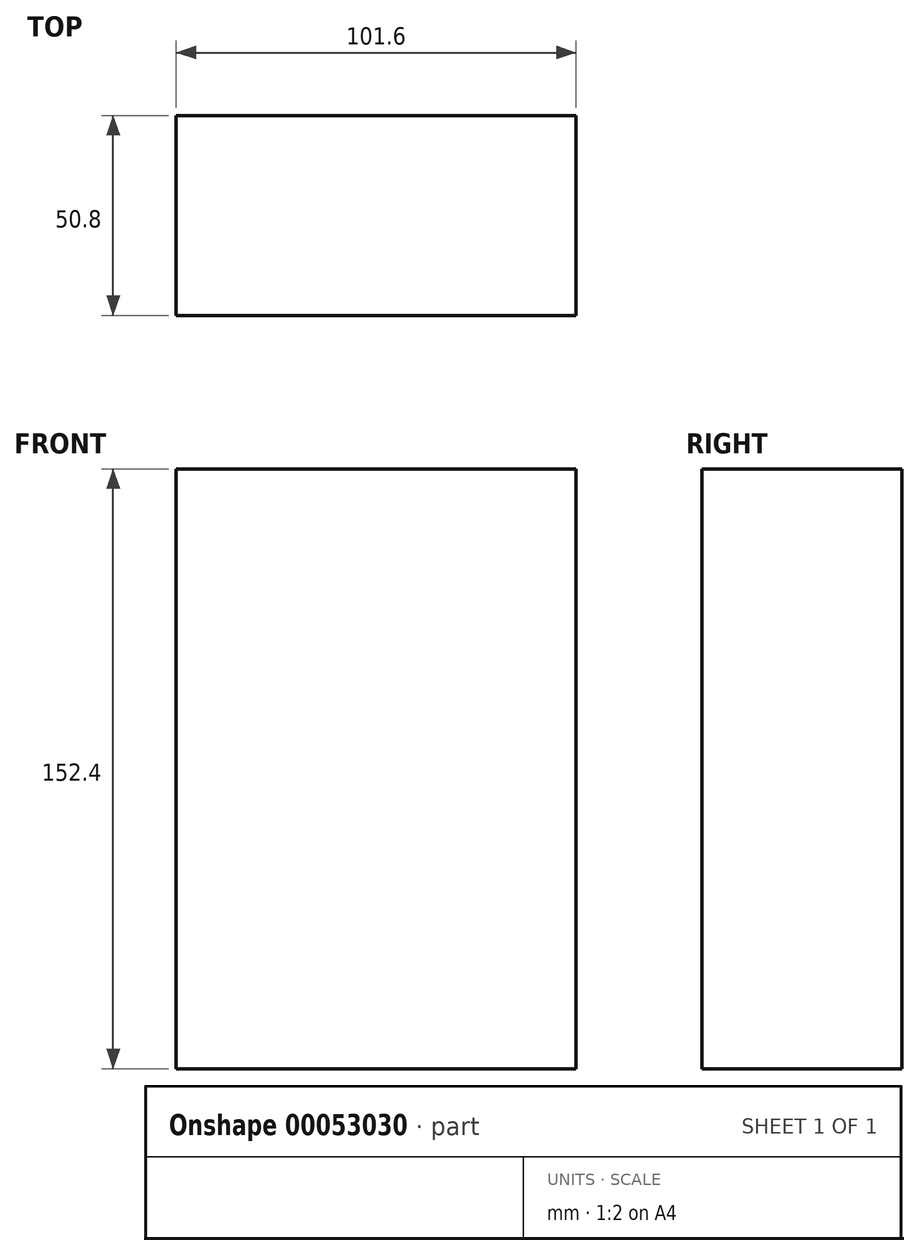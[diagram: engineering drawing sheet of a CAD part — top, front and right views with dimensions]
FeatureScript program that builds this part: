
annotation { "Feature Type Name" : "Feature", "Feature Type Description" : "" }
export const myFeature = defineFeature(function(context is Context, id is Id, definition is map)
    precondition{}
    {
        {
            var Q0;
            Q0=qCreatedBy(makeId("Top.planeOp"),FACE);
            var sketch = newSketch(context, id + "F0", { "sketchPlane" : qUnion([Q0])});
            skLineSegment(sketch, "E0.bottom", {"start": v(0, 0) * mm, "end": v(-101.6, 0) * mm});
            skLineSegment(sketch, "E0.top", {"start": v(0, 50.8) * mm, "end": v(-101.6, 50.8) * mm});
            skLineSegment(sketch, "E0.left", {"start": v(0, 0) * mm, "end": v(0, 50.8) * mm});
            skLineSegment(sketch, "E0.right", {"start": v(-101.6, 0) * mm, "end": v(-101.6, 50.8) * mm});
            skSolve(sketch);
        }
        {
            var Q0;
            Q0 = qSketchRegion(id + "F0", true);
            extrude(context, id + "F1", {"entities" : qUnion([Q0]), "depth" : 152.4 * mm});
        }
    });
